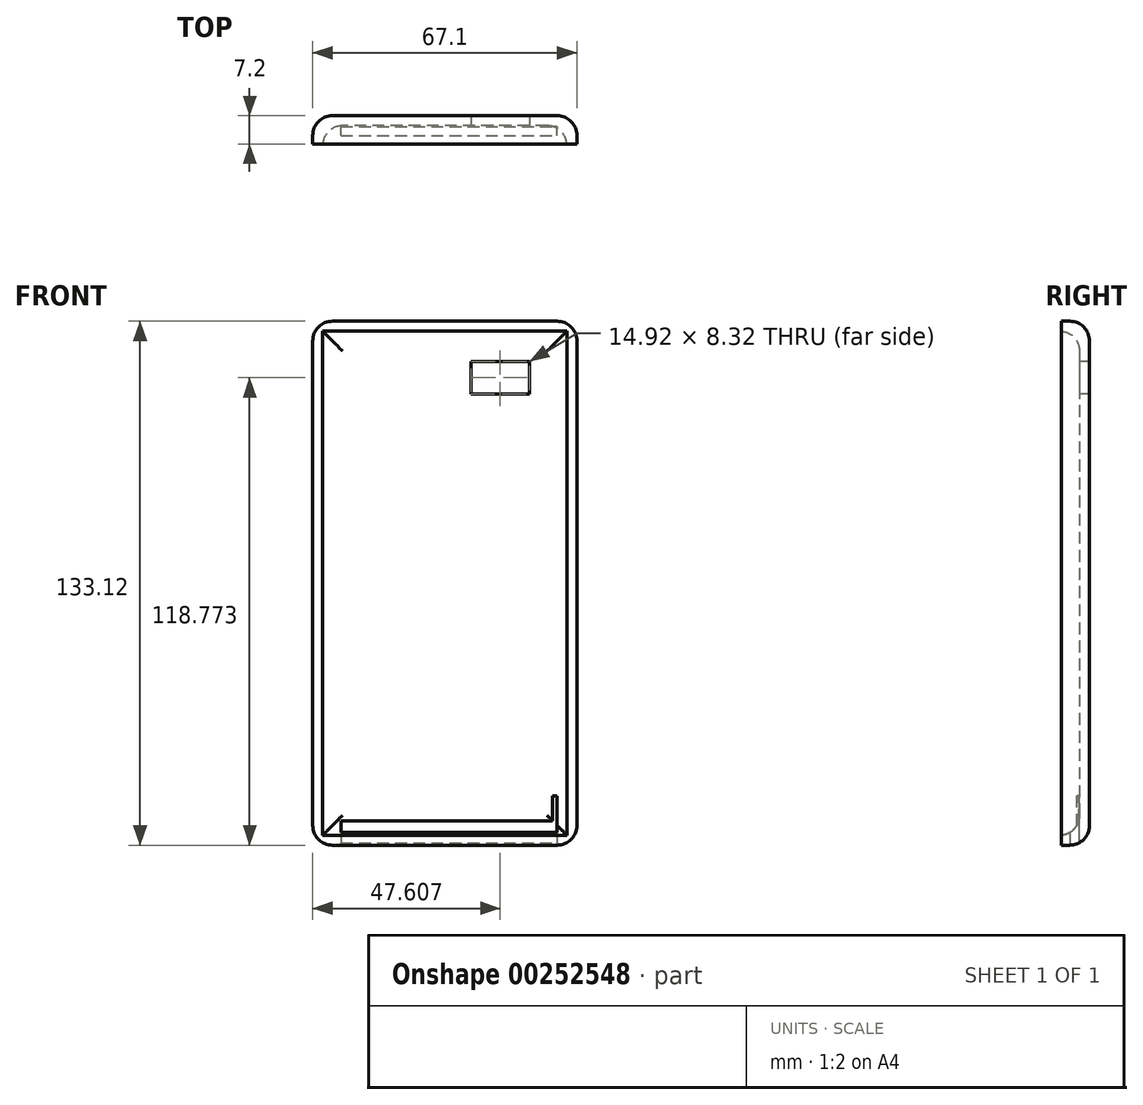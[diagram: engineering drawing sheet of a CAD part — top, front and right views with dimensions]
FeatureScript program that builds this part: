
annotation { "Feature Type Name" : "Feature", "Feature Type Description" : "" }
export const myFeature = defineFeature(function(context is Context, id is Id, definition is map)
    precondition{}
    {
        {
            var Q0;
            Q0=qCreatedBy(makeId("Front.planeOp"),FACE);
            var sketch = newSketch(context, id + "F0", { "sketchPlane" : qUnion([Q0])});
            skLineSegment(sketch, "E0.bottom", {"start": v(-33.55, -66.56) * mm, "end": v(33.55, -66.56) * mm});
            skLineSegment(sketch, "E0.top", {"start": v(-33.55, 66.56) * mm, "end": v(33.55, 66.56) * mm});
            skLineSegment(sketch, "E0.left", {"start": v(-33.55, -66.56) * mm, "end": v(-33.55, 66.56) * mm});
            skLineSegment(sketch, "E0.right", {"start": v(33.55, -66.56) * mm, "end": v(33.55, 66.56) * mm});
            skPoint(sketch, "E0.middle", {"position": v(0, 0) * mm});
            skSolve(sketch);
        }
        {
            var Q0;
            Q0=makeQuery(id+"F0.imprint","IMPRINT",FACE,{"disambiguationData":[TD([[makeQuery(id+"F0.imprint","IMPRINT",EDGE,{"derivedFrom":sQuery(id+"F0.wireOp",EDGE,"E0.bottom")}),1.0]])]});
            extrude(context, id + "F1", {"entities" : qUnion([Q0]), "depth" : 7.2 * mm});
        }
        {
            var Q0;
            Q0=makeQuery(id+"F1.opExtrude","CAP_FACE",FACE,{"disambiguationData":[OSD([sQuery(id+"F0.wireOp",EDGE,"E0.bottom"),sQuery(id+"F0.wireOp",EDGE,"E0.top"),sQuery(id+"F0.wireOp",EDGE,"E0.left"),sQuery(id+"F0.wireOp",EDGE,"E0.right")])],"isStart":false});
            shell(context, id + "F2", {"entities" : qUnion([Q0]), "thickness" : 2.54 * mm});
        }
        {
            var Q0;
            Q0=makeQuery(id+"F2.opShell","OFFSET_FACE",FACE,{"disambiguationData":[OSD([sQuery(id+"F0.wireOp",EDGE,"E0.bottom"),sQuery(id+"F0.wireOp",EDGE,"E0.top"),sQuery(id+"F0.wireOp",EDGE,"E0.left"),sQuery(id+"F0.wireOp",EDGE,"E0.right")])]});
            var Q1;
            Q1=makeQuery(id+"F1.opExtrude","CAP_FACE",FACE,{"disambiguationData":[OSD([sQuery(id+"F0.wireOp",EDGE,"E0.bottom"),sQuery(id+"F0.wireOp",EDGE,"E0.top"),sQuery(id+"F0.wireOp",EDGE,"E0.left"),sQuery(id+"F0.wireOp",EDGE,"E0.right")])],"isStart":true});
            var Q2;
            Q2=makeQuery(id+"F1.opExtrude","SWEPT_EDGE",EDGE,{"disambiguationData":[OSD([sQuery(id+"F0.wireOp",EDGE,"E0.top"),sQuery(id+"F0.wireOp",EDGE,"E0.right")])]});
            var Q3;
            Q3=makeQuery(id+"F1.opExtrude","SWEPT_EDGE",EDGE,{"disambiguationData":[OSD([sQuery(id+"F0.wireOp",EDGE,"E0.top"),sQuery(id+"F0.wireOp",EDGE,"E0.left")])]});
            var Q4;
            Q4=makeQuery(id+"F1.opExtrude","SWEPT_EDGE",EDGE,{"disambiguationData":[OSD([sQuery(id+"F0.wireOp",EDGE,"E0.bottom"),sQuery(id+"F0.wireOp",EDGE,"E0.left")])]});
            var Q5;
            Q5=makeQuery(id+"F1.opExtrude","SWEPT_EDGE",EDGE,{"disambiguationData":[OSD([sQuery(id+"F0.wireOp",EDGE,"E0.bottom"),sQuery(id+"F0.wireOp",EDGE,"E0.right")])]});
            fillet(context, id + "F3", {"entities" : qUnion([Q0, Q1, Q2, Q3, Q4, Q5]), "radius" : 5 * mm, "tangentPropagation" : true, "allowEdgeOverflow" : false});
        }
        {
            var Q0;
            Q0=makeQuery(id+"F2.opShell","OFFSET_FACE",FACE,{"disambiguationData":[OSD([sQuery(id+"F0.wireOp",EDGE,"E0.bottom"),sQuery(id+"F0.wireOp",EDGE,"E0.top"),sQuery(id+"F0.wireOp",EDGE,"E0.left"),sQuery(id+"F0.wireOp",EDGE,"E0.right")])]});
            var sketch = newSketch(context, id + "F4", { "sketchPlane" : qUnion([Q0])});
            skLineSegment(sketch, "E1.bottom", {"start": v(21.52, 56.37) * mm, "end": v(6.6, 56.37) * mm});
            skLineSegment(sketch, "E1.top", {"start": v(21.52, 48.05) * mm, "end": v(6.6, 48.05) * mm});
            skLineSegment(sketch, "E1.left", {"start": v(21.52, 56.37) * mm, "end": v(21.52, 48.05) * mm});
            skLineSegment(sketch, "E1.right", {"start": v(6.6, 56.37) * mm, "end": v(6.6, 48.05) * mm});
            skSolve(sketch);
        }
        {
            var Q0;
            Q0=makeQuery(id+"F4.imprint","IMPRINT",FACE,{"disambiguationData":[TD([[makeQuery(id+"F4.imprint","IMPRINT",EDGE,{"derivedFrom":sQuery(id+"F4.wireOp",EDGE,"E1.bottom")}),1.0]])]});
            extrude(context, id + "F5", {"entities" : qUnion([Q0]), "operationType" : NewBodyOperationType.REMOVE, "endBound" : BoundingType.SYMMETRIC, "oppositeDirection" : true, "depth" : 25 * mm});
        }
        {
            var Q0;
            Q0=makeQuery(id+"F1.opExtrude","SWEPT_FACE",FACE,{"disambiguationData":[OSD([sQuery(id+"F0.wireOp",EDGE,"E0.bottom")])]});
            var sketch = newSketch(context, id + "F6", { "sketchPlane" : qUnion([Q0])});
            skLineSegment(sketch, "E2.bottom", {"start": v(28.55, 2.73) * mm, "end": v(-26.4, 2.73) * mm});
            skLineSegment(sketch, "E2.top", {"start": v(28.55, 5) * mm, "end": v(-26.4, 5) * mm});
            skLineSegment(sketch, "E2.left", {"start": v(28.55, 2.73) * mm, "end": v(28.55, 5) * mm});
            skLineSegment(sketch, "E2.right", {"start": v(-26.4, 2.73) * mm, "end": v(-26.4, 5) * mm});
            skSolve(sketch);
        }
        {
            var Q0;
            Q0=qSketchRegion(id+"F6",true);
            extrude(context, id + "F7", {"entities" : qUnion([Q0]), "operationType" : NewBodyOperationType.REMOVE, "endBound" : BoundingType.SYMMETRIC, "oppositeDirection" : true, "depth" : 25 * mm});
        }
    });
